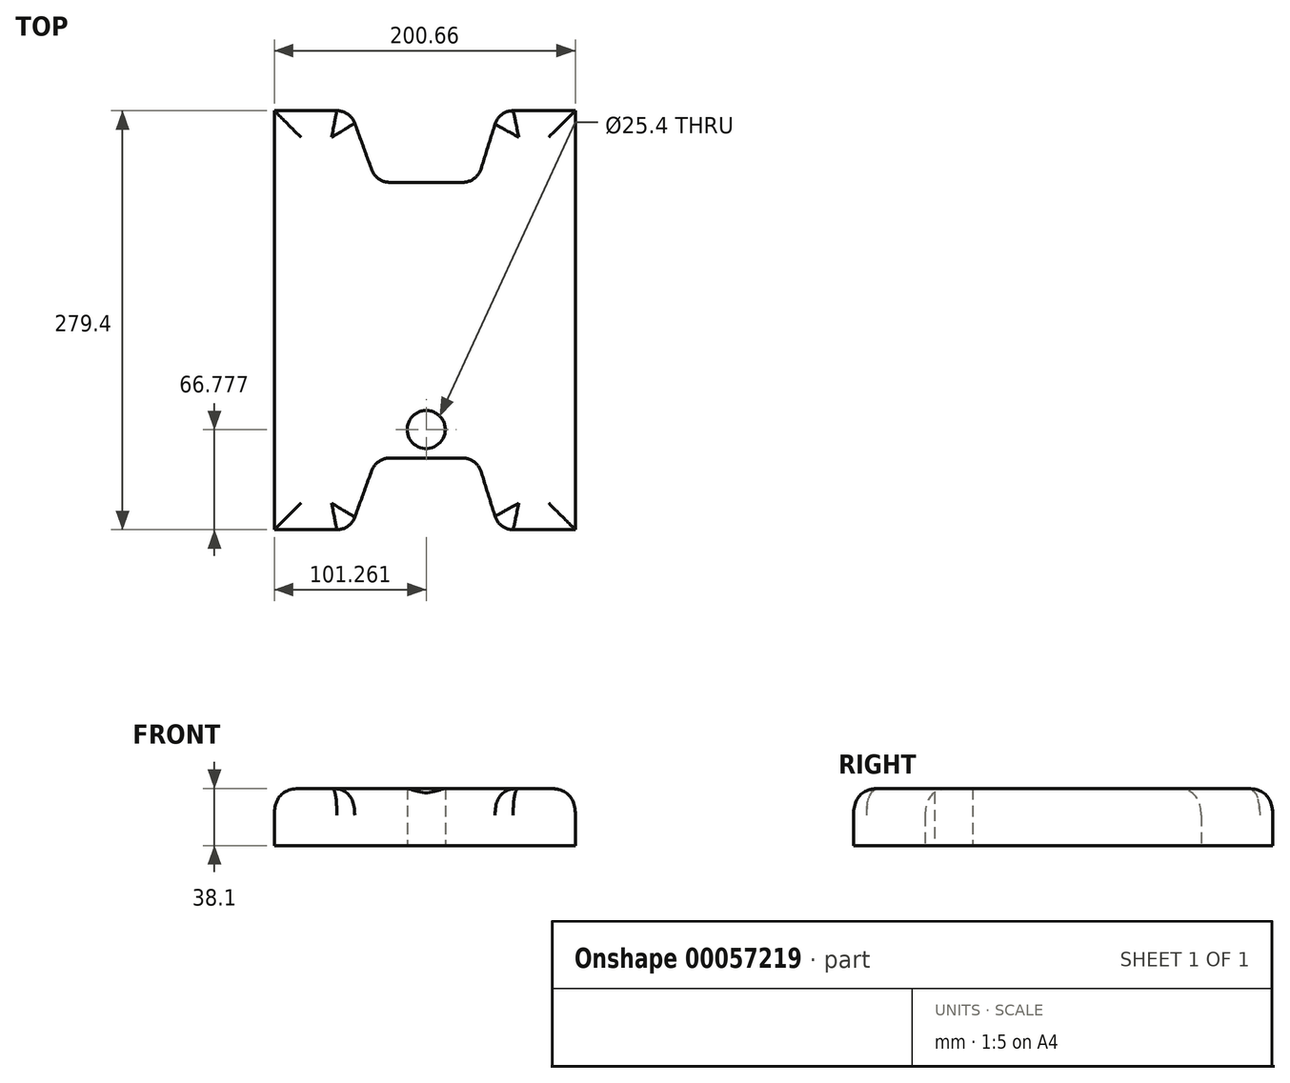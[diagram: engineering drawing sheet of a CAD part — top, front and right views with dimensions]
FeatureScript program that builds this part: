
annotation { "Feature Type Name" : "Feature", "Feature Type Description" : "" }
export const myFeature = defineFeature(function(context is Context, id is Id, definition is map)
    precondition{}
    {
        {
            var Q0;
            Q0=qCreatedBy(makeId("Top.planeOp"),FACE);
            var sketch = newSketch(context, id + "F0", { "sketchPlane" : qUnion([Q0])});
            skLineSegment(sketch, "E0.bottom", {"start": v(-107.95, 139.7) * mm, "end": v(-66.27, 139.7) * mm});
            skLineSegment(sketch, "E0.top", {"start": v(-107.95, -139.7) * mm, "end": v(-66.27, -139.7) * mm});
            skLineSegment(sketch, "E0.left", {"start": v(-107.95, 139.7) * mm, "end": v(-107.95, -139.7) * mm});
            skLineSegment(sketch, "E0.right", {"start": v(92.71, 139.7) * mm, "end": v(92.71, -139.7) * mm});
            skLineSegment(sketch, "E1", {"start": v(-31.1, -91.97) * mm, "end": v(17.71, -91.97) * mm});
            skLineSegment(sketch, "E2", {"start": v(-54.33, -131.35) * mm, "end": v(-43.02, -100.32) * mm});
            skLineSegment(sketch, "E3", {"start": v(29.84, -100.89) * mm, "end": v(39.18, -130.79) * mm});
            skLineSegment(sketch, "E4.MirrorCS", {"start": v(-31.1, 91.97) * mm, "end": v(17.71, 91.97) * mm});
            skLineSegment(sketch, "E5.MirrorCS", {"start": v(-54.33, 131.35) * mm, "end": v(-43.02, 100.32) * mm});
            skLineSegment(sketch, "E6.MirrorCS", {"start": v(29.84, 100.89) * mm, "end": v(39.18, 130.79) * mm});
            skPoint(sketch, "E7.visualSharp", {"position": v(-39.98, -91.97) * mm});
            skArc(sketch, "E7.filletArc", {"start": v(-31.1, -91.97) * mm, "mid": v(-38.37, -94.27) * mm, "end": v(-43.02, -100.32) * mm});
            skPoint(sketch, "E8.visualSharp", {"position": v(27.05, -91.97) * mm});
            skArc(sketch, "E8.filletArc", {"start": v(29.84, -100.89) * mm, "mid": v(25.24, -94.44) * mm, "end": v(17.71, -91.97) * mm});
            skPoint(sketch, "E9.newPointB", {"position": v(-57.38, -139.7) * mm});
            skArc(sketch, "E9.filletArc", {"start": v(-66.27, -139.7) * mm, "mid": v(-58.98, -137.4) * mm, "end": v(-54.33, -131.35) * mm});
            skLineSegment(sketch, "E10", {"start": v(92.71, -139.7) * mm, "end": v(51.3, -139.7) * mm});
            skPoint(sketch, "E11.visualSharp", {"position": v(41.96, -139.7) * mm});
            skArc(sketch, "E11.filletArc", {"start": v(39.18, -130.79) * mm, "mid": v(43.78, -137.23) * mm, "end": v(51.3, -139.7) * mm});
            skPoint(sketch, "E12.visualSharp", {"position": v(27.05, 91.97) * mm});
            skArc(sketch, "E12.filletArc", {"start": v(17.71, 91.97) * mm, "mid": v(25.24, 94.44) * mm, "end": v(29.84, 100.89) * mm});
            skPoint(sketch, "E13.visualSharp", {"position": v(-39.98, 91.97) * mm});
            skArc(sketch, "E13.filletArc", {"start": v(-43.02, 100.32) * mm, "mid": v(-38.37, 94.27) * mm, "end": v(-31.1, 91.97) * mm});
            skPoint(sketch, "E14.newPointA", {"position": v(-57.38, 139.7) * mm});
            skPoint(sketch, "E14.newPointB", {"position": v(92.71, 139.7) * mm});
            skArc(sketch, "E14.filletArc", {"start": v(-54.33, 131.35) * mm, "mid": v(-58.98, 137.4) * mm, "end": v(-66.27, 139.7) * mm});
            skLineSegment(sketch, "E15", {"start": v(92.71, 139.7) * mm, "end": v(51.3, 139.7) * mm});
            skPoint(sketch, "E16.visualSharp", {"position": v(41.96, 139.7) * mm});
            skArc(sketch, "E16.filletArc", {"start": v(51.3, 139.7) * mm, "mid": v(43.78, 137.23) * mm, "end": v(39.18, 130.79) * mm});
            skCircle(sketch, "E17", {"center": v(-6.69, -72.92) * mm, "radius": 12.7 * mm});
            skPoint(sketch, "E17.centerSnap0", {"position": v(-6.69, -91.97) * mm});
            skSolve(sketch);
        }
        {
            var Q0;
            Q0=makeQuery(id+"F0.imprint","IMPRINT",FACE,{"disambiguationData":[TD([[makeQuery(id+"F0.imprint","IMPRINT",EDGE,{"derivedFrom":sQuery(id+"F0.wireOp",EDGE,"E0.bottom")}),-1.0]])]});
            extrude(context, id + "F1", {"entities" : qUnion([Q0]), "depth" : 38.1 * mm});
        }
        {
            var Q0;
            Q0=makeQuery(id+"F1.opExtrude","CAP_EDGE",EDGE,{"disambiguationData":[OSD([sQuery(id+"F0.wireOp",EDGE,"E0.right")])],"isStart":false});
            var Q1;
            Q1=makeQuery(id+"F1.opExtrude","CAP_EDGE",EDGE,{"disambiguationData":[OSD([sQuery(id+"F0.wireOp",EDGE,"E0.bottom")])],"isStart":false});
            var Q2;
            Q2=makeQuery(id+"F1.opExtrude","CAP_EDGE",EDGE,{"disambiguationData":[OSD([sQuery(id+"F0.wireOp",EDGE,"E0.left")])],"isStart":false});
            var Q3;
            Q3=makeQuery(id+"F1.opExtrude","CAP_EDGE",EDGE,{"disambiguationData":[OSD([sQuery(id+"F0.wireOp",EDGE,"E0.top")])],"isStart":false});
            var Q4;
            Q4=makeQuery(id+"F1.opExtrude","CAP_EDGE",EDGE,{"disambiguationData":[OSD([sQuery(id+"F0.wireOp",EDGE,"E2")])],"isStart":false});
            var Q5;
            Q5=makeQuery(id+"F1.opExtrude","CAP_EDGE",EDGE,{"disambiguationData":[OSD([sQuery(id+"F0.wireOp",EDGE,"E1")])],"isStart":false});
            var Q6;
            Q6=makeQuery(id+"F1.opExtrude","CAP_EDGE",EDGE,{"disambiguationData":[OSD([sQuery(id+"F0.wireOp",EDGE,"E3")])],"isStart":false});
            var Q7;
            Q7=makeQuery(id+"F1.opExtrude","CAP_EDGE",EDGE,{"disambiguationData":[OSD([sQuery(id+"F0.wireOp",EDGE,"E6.MirrorCS")])],"isStart":false});
            var Q8;
            Q8=makeQuery(id+"F1.opExtrude","CAP_EDGE",EDGE,{"disambiguationData":[OSD([sQuery(id+"F0.wireOp",EDGE,"E4.MirrorCS")])],"isStart":false});
            var Q9;
            Q9=makeQuery(id+"F1.opExtrude","CAP_EDGE",EDGE,{"disambiguationData":[OSD([sQuery(id+"F0.wireOp",EDGE,"E5.MirrorCS")])],"isStart":false});
            fillet(context, id + "F2", {"entities" : qUnion([Q0, Q1, Q2, Q3, Q4, Q5, Q6, Q7, Q8, Q9]), "radius" : 17.78 * mm, "tangentPropagation" : true, "rho" : 0.5, "crossSection" : FilletCrossSection.CONIC, "allowEdgeOverflow" : false});
        }
    });
